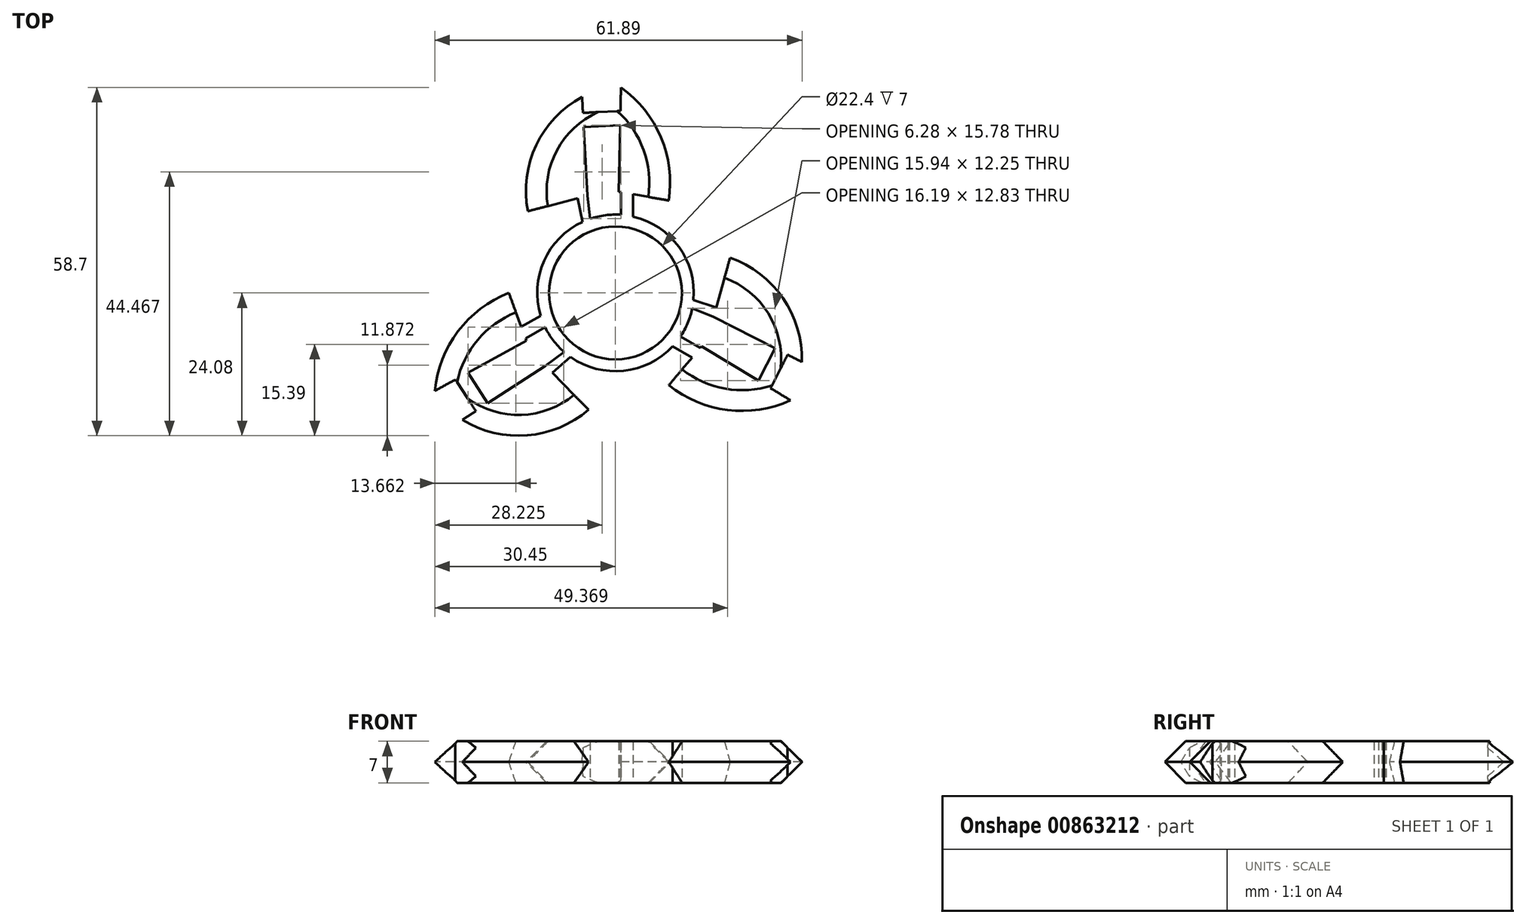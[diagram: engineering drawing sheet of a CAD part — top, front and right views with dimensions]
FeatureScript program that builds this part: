
annotation { "Feature Type Name" : "Feature", "Feature Type Description" : "" }
export const myFeature = defineFeature(function(context is Context, id is Id, definition is map)
    precondition{}
    {
        {
            var Q0;
            Q0=qCreatedBy(makeId("Top.planeOp"),FACE);
            var sketch = newSketch(context, id + "F0", { "sketchPlane" : qUnion([Q0])});
            skCircle(sketch, "E0", {"center": v(0, 0) * mm, "radius": 11.2 * mm});
            skCircle(sketch, "E1", {"center": v(0, 0) * mm, "radius": 13.2 * mm});
            skLineSegment(sketch, "E2", {"start": v(-11.8, -12.3) * mm, "end": v(-4.52, -19.69) * mm});
            skLineSegment(sketch, "E3", {"start": v(-15.03, -8.08) * mm, "end": v(-17.98, 0) * mm});
            skLineSegment(sketch, "E4", {"start": v(-15.03, -8.08) * mm, "end": v(-30.45, -16.5) * mm});
            skLineSegment(sketch, "E5", {"start": v(-11.8, -12.3) * mm, "end": v(-25.8, -21.4) * mm});
            skArc(sketch, "E6", {"start": v(-17.98, 0) * mm, "mid": v(-26.55, -6.49) * mm, "end": v(-30.45, -16.5) * mm});
            skArc(sketch, "E7", {"start": v(-25.8, -21.4) * mm, "mid": v(-14.88, -24.02) * mm, "end": v(-4.52, -19.69) * mm});
            skLineSegment(sketch, "E8.1.0", {"start": v(14.51, -8.98) * mm, "end": v(8.99, -15.57) * mm});
            skArc(sketch, "E8.1.3", {"start": v(8.99, -15.57) * mm, "mid": v(18.9, -19.75) * mm, "end": v(29.52, -18.11) * mm});
            skLineSegment(sketch, "E8.1.4", {"start": v(14.51, -8.98) * mm, "end": v(29.52, -18.11) * mm});
            skLineSegment(sketch, "E8.1.5", {"start": v(16.55, -4.07) * mm, "end": v(31.43, -11.65) * mm});
            skLineSegment(sketch, "E8.1.7", {"start": v(16.55, -4.07) * mm, "end": v(19.31, 5.93) * mm});
            skArc(sketch, "E8.1.9", {"start": v(31.43, -11.65) * mm, "mid": v(28.24, -0.88) * mm, "end": v(19.31, 5.93) * mm});
            skLineSegment(sketch, "E8.2.0", {"start": v(0.52, 17.06) * mm, "end": v(8.99, 15.57) * mm});
            skArc(sketch, "E8.2.3", {"start": v(8.99, 15.57) * mm, "mid": v(7.65, 26.24) * mm, "end": v(0.93, 34.62) * mm});
            skLineSegment(sketch, "E8.2.4", {"start": v(0.52, 17.06) * mm, "end": v(0.93, 34.62) * mm});
            skLineSegment(sketch, "E8.2.5", {"start": v(-4.75, 16.37) * mm, "end": v(-5.63, 33.04) * mm});
            skLineSegment(sketch, "E8.2.7", {"start": v(-4.75, 16.37) * mm, "end": v(-14.79, 13.76) * mm});
            skArc(sketch, "E8.2.9", {"start": v(-5.63, 33.04) * mm, "mid": v(-13.36, 24.9) * mm, "end": v(-14.79, 13.76) * mm});
            skPoint(sketch, "E9.end.orphan", {"position": v(-15.78, -5.85) * mm});
            skPoint(sketch, "E10.start.orphan", {"position": v(-11.83, -5.85) * mm});
            skPoint(sketch, "E11.startSnap0", {"position": v(4.76, 16.31) * mm});
            skPoint(sketch, "E12.orphan", {"position": v(-9.55, -5.85) * mm});
            skPoint(sketch, "E13.end.orphan", {"position": v(13.36, -14.64) * mm});
            skPoint(sketch, "E11.start.orphan", {"position": v(4.76, 17.14) * mm});
            skLineSegment(sketch, "E14", {"start": v(0.91, 17.67) * mm, "end": v(0.91, 12.44) * mm});
            skLineSegment(sketch, "E15", {"start": v(2.98, 17.14) * mm, "end": v(2.98, 12.22) * mm});
            skLineSegment(sketch, "E16", {"start": v(-4.75, 16.37) * mm, "end": v(-4.13, 11.53) * mm});
            skLineSegment(sketch, "E17", {"start": v(-5.43, 11.37) * mm, "end": v(-6.5, 16.65) * mm});
            skLineSegment(sketch, "E18.1.0", {"start": v(-11.8, -12.3) * mm, "end": v(-7.92, -9.34) * mm});
            skLineSegment(sketch, "E18.1.1", {"start": v(-7.13, -10.4) * mm, "end": v(-11.17, -13.96) * mm});
            skLineSegment(sketch, "E18.2.0", {"start": v(16.55, -4.07) * mm, "end": v(12.05, -2.19) * mm});
            skLineSegment(sketch, "E18.2.1", {"start": v(12.57, -0.98) * mm, "end": v(17.67, -2.7) * mm});
            skLineSegment(sketch, "E19.1.0", {"start": v(-15.76, -8.05) * mm, "end": v(-11.23, -5.43) * mm});
            skLineSegment(sketch, "E19.1.1", {"start": v(-16.33, -6) * mm, "end": v(-12.07, -3.53) * mm});
            skLineSegment(sketch, "E19.2.0", {"start": v(14.85, -9.63) * mm, "end": v(10.32, -7.01) * mm});
            skLineSegment(sketch, "E19.2.1", {"start": v(13.36, -11.15) * mm, "end": v(9.1, -8.68) * mm});
            skLineSegment(sketch, "E20", {"start": v(0.84, 30.67) * mm, "end": v(-5.49, 30.34) * mm});
            skLineSegment(sketch, "E21", {"start": v(-5.36, 27.95) * mm, "end": v(0.78, 28.28) * mm});
            skLineSegment(sketch, "E22.1.0", {"start": v(-26.98, -14.61) * mm, "end": v(-23.53, -19.92) * mm});
            skLineSegment(sketch, "E22.1.1", {"start": v(-21.53, -18.62) * mm, "end": v(-24.88, -13.46) * mm});
            skLineSegment(sketch, "E22.2.0", {"start": v(26.15, -16.06) * mm, "end": v(29.02, -10.42) * mm});
            skLineSegment(sketch, "E22.2.1", {"start": v(26.9, -9.33) * mm, "end": v(24.1, -14.82) * mm});
            skSolve(sketch);
        }
        {
            var Q0;
            {var subQ0=sQuery(id+"F0.wireOp",EDGE,"E20");Q0=makeQuery(id+"F0.imprint","IMPRINT",FACE,{"disambiguationData":[TD([[makeQuery(id+"F0.imprint","IMPRINT",EDGE,{"derivedFrom":subQ0}),1.0]])]});}
            var Q1;
            {var subQ4=sQuery(id+"F0.wireOp",EDGE,"E8.2.9");Q1=makeQuery(id+"F0.imprint","IMPRINT",FACE,{"disambiguationData":[TD([[makeQuery(id+"F0.imprint","IMPRINT",EDGE,{"derivedFrom":subQ4}),1.0]])]});}
            var Q2;
            {var subQ0=sQuery(id+"F0.wireOp",EDGE,"E17");var subQ1=sQuery(id+"F0.wireOp",EDGE,"E1");var subQ2=makeQuery(id+"F0.imprint","INTERSECT",VERTEX,{"derivedFrom":[subQ1,subQ0]});Q2=makeQuery(id+"F0.imprint","IMPRINT",FACE,{"disambiguationData":[TD([[makeQuery(id+"F0.imprint","IMPRINT",EDGE,{"disambiguationData":[TD([[subQ2,1.0]])],"derivedFrom":subQ1}),-1.0]])]});}
            var Q3;
            {var subQ0=sQuery(id+"F0.wireOp",EDGE,"E8.2.3");Q3=makeQuery(id+"F0.imprint","IMPRINT",FACE,{"disambiguationData":[TD([[makeQuery(id+"F0.imprint","IMPRINT",EDGE,{"derivedFrom":subQ0}),1.0]])]});}
            var Q4;
            {var subQ0=sQuery(id+"F0.wireOp",EDGE,"E15");var subQ1=sQuery(id+"F0.wireOp",EDGE,"E1");var subQ2=makeQuery(id+"F0.imprint","INTERSECT",VERTEX,{"derivedFrom":[subQ1,subQ0]});Q4=makeQuery(id+"F0.imprint","IMPRINT",FACE,{"disambiguationData":[TD([[makeQuery(id+"F0.imprint","IMPRINT",EDGE,{"disambiguationData":[TD([[subQ2,-1.0]])],"derivedFrom":subQ1}),-1.0]])]});}
            var Q5;
            Q5=makeQuery(id+"F0.imprint","IMPRINT",FACE,{"disambiguationData":[TD([[makeQuery(id+"F0.imprint","IMPRINT",EDGE,{"derivedFrom":sQuery(id+"F0.wireOp",EDGE,"E0")}),-1.0]])]});
            var Q6;
            {var subQ4=sQuery(id+"F0.wireOp",EDGE,"E6");Q6=makeQuery(id+"F0.imprint","IMPRINT",FACE,{"disambiguationData":[TD([[makeQuery(id+"F0.imprint","IMPRINT",EDGE,{"derivedFrom":subQ4}),1.0]])]});}
            var Q7;
            {var subQ0=sQuery(id+"F0.wireOp",EDGE,"E19.1.1");var subQ1=sQuery(id+"F0.wireOp",EDGE,"E1");var subQ2=makeQuery(id+"F0.imprint","INTERSECT",VERTEX,{"derivedFrom":[subQ1,subQ0]});Q7=makeQuery(id+"F0.imprint","IMPRINT",FACE,{"disambiguationData":[TD([[makeQuery(id+"F0.imprint","IMPRINT",EDGE,{"disambiguationData":[TD([[subQ2,-1.0]])],"derivedFrom":subQ1}),-1.0]])]});}
            var Q8;
            {var subQ0=sQuery(id+"F0.wireOp",EDGE,"E18.1.1");var subQ1=sQuery(id+"F0.wireOp",EDGE,"E1");var subQ2=makeQuery(id+"F0.imprint","INTERSECT",VERTEX,{"derivedFrom":[subQ1,subQ0]});Q8=makeQuery(id+"F0.imprint","IMPRINT",FACE,{"disambiguationData":[TD([[makeQuery(id+"F0.imprint","IMPRINT",EDGE,{"disambiguationData":[TD([[subQ2,1.0]])],"derivedFrom":subQ1}),-1.0]])]});}
            var Q9;
            {var subQ5=sQuery(id+"F0.wireOp",EDGE,"E7");Q9=makeQuery(id+"F0.imprint","IMPRINT",FACE,{"disambiguationData":[TD([[makeQuery(id+"F0.imprint","IMPRINT",EDGE,{"derivedFrom":subQ5}),1.0]])]});}
            var Q10;
            {var subQ0=sQuery(id+"F0.wireOp",EDGE,"E22.1.0");Q10=makeQuery(id+"F0.imprint","IMPRINT",FACE,{"disambiguationData":[TD([[makeQuery(id+"F0.imprint","IMPRINT",EDGE,{"derivedFrom":subQ0}),1.0]])]});}
            var Q11;
            {var subQ0=sQuery(id+"F0.wireOp",EDGE,"E19.2.1");var subQ1=sQuery(id+"F0.wireOp",EDGE,"E1");var subQ2=makeQuery(id+"F0.imprint","INTERSECT",VERTEX,{"derivedFrom":[subQ1,subQ0]});Q11=makeQuery(id+"F0.imprint","IMPRINT",FACE,{"disambiguationData":[TD([[makeQuery(id+"F0.imprint","IMPRINT",EDGE,{"disambiguationData":[TD([[subQ2,-1.0]])],"derivedFrom":subQ1}),-1.0]])]});}
            var Q12;
            {var subQ0=sQuery(id+"F0.wireOp",EDGE,"E8.1.3");Q12=makeQuery(id+"F0.imprint","IMPRINT",FACE,{"disambiguationData":[TD([[makeQuery(id+"F0.imprint","IMPRINT",EDGE,{"derivedFrom":subQ0}),1.0]])]});}
            var Q13;
            {var subQ0=sQuery(id+"F0.wireOp",EDGE,"E22.2.0");Q13=makeQuery(id+"F0.imprint","IMPRINT",FACE,{"disambiguationData":[TD([[makeQuery(id+"F0.imprint","IMPRINT",EDGE,{"derivedFrom":subQ0}),1.0]])]});}
            var Q14;
            {var subQ4=sQuery(id+"F0.wireOp",EDGE,"E8.1.9");Q14=makeQuery(id+"F0.imprint","IMPRINT",FACE,{"disambiguationData":[TD([[makeQuery(id+"F0.imprint","IMPRINT",EDGE,{"derivedFrom":subQ4}),1.0]])]});}
            var Q15;
            {var subQ0=sQuery(id+"F0.wireOp",EDGE,"E18.2.1");var subQ1=sQuery(id+"F0.wireOp",EDGE,"E1");var subQ2=makeQuery(id+"F0.imprint","INTERSECT",VERTEX,{"derivedFrom":[subQ1,subQ0]});Q15=makeQuery(id+"F0.imprint","IMPRINT",FACE,{"disambiguationData":[TD([[makeQuery(id+"F0.imprint","IMPRINT",EDGE,{"disambiguationData":[TD([[subQ2,1.0]])],"derivedFrom":subQ1}),-1.0]])]});}
            extrude(context, id + "F1", {"entities" : qUnion([Q0, Q1, Q2, Q3, Q4, Q5, Q6, Q7, Q8, Q9, Q10, Q11, Q12, Q13, Q14, Q15]), "depth" : 7 * mm, "offsetDistance" : 25 * mm});
        }
        {
            var Q0;
            Q0=makeQuery(id+"F1.opExtrude","CAP_EDGE",EDGE,{"disambiguationData":[OSD([sQuery(id+"F0.wireOp",EDGE,"E8.2.9")])],"isStart":false});
            var Q1;
            Q1=makeQuery(id+"F1.opExtrude","CAP_EDGE",EDGE,{"disambiguationData":[OSD([sQuery(id+"F0.wireOp",EDGE,"E8.2.3")])],"isStart":false});
            var Q2;
            Q2=makeQuery(id+"F1.opExtrude","CAP_EDGE",EDGE,{"disambiguationData":[OSD([sQuery(id+"F0.wireOp",EDGE,"E8.1.9")])],"isStart":false});
            var Q3;
            Q3=makeQuery(id+"F1.opExtrude","CAP_EDGE",EDGE,{"disambiguationData":[OSD([sQuery(id+"F0.wireOp",EDGE,"E8.1.3")])],"isStart":false});
            var Q4;
            Q4=makeQuery(id+"F1.opExtrude","CAP_EDGE",EDGE,{"disambiguationData":[OSD([sQuery(id+"F0.wireOp",EDGE,"E7")])],"isStart":false});
            var Q5;
            Q5=makeQuery(id+"F1.opExtrude","CAP_EDGE",EDGE,{"disambiguationData":[OSD([sQuery(id+"F0.wireOp",EDGE,"E6")])],"isStart":false});
            chamfer(context, id + "F2", {"entities" : qUnion([Q0, Q1, Q2, Q3, Q4, Q5]), "width" : 3.5 * mm, "tangentPropagation" : true});
        }
        {
            var Q0;
            Q0=makeQuery(id+"F1.opExtrude","CAP_EDGE",EDGE,{"disambiguationData":[OSD([sQuery(id+"F0.wireOp",EDGE,"E8.2.3")])],"isStart":true});
            var Q1;
            Q1=makeQuery(id+"F1.opExtrude","CAP_EDGE",EDGE,{"disambiguationData":[OSD([sQuery(id+"F0.wireOp",EDGE,"E8.2.9")])],"isStart":true});
            var Q2;
            Q2=makeQuery(id+"F1.opExtrude","CAP_EDGE",EDGE,{"disambiguationData":[OSD([sQuery(id+"F0.wireOp",EDGE,"E6")])],"isStart":true});
            var Q3;
            Q3=makeQuery(id+"F1.opExtrude","CAP_EDGE",EDGE,{"disambiguationData":[OSD([sQuery(id+"F0.wireOp",EDGE,"E7")])],"isStart":true});
            var Q4;
            Q4=makeQuery(id+"F1.opExtrude","CAP_EDGE",EDGE,{"disambiguationData":[OSD([sQuery(id+"F0.wireOp",EDGE,"E8.1.3")])],"isStart":true});
            var Q5;
            Q5=makeQuery(id+"F1.opExtrude","CAP_EDGE",EDGE,{"disambiguationData":[OSD([sQuery(id+"F0.wireOp",EDGE,"E8.1.9")])],"isStart":true});
            chamfer(context, id + "F3", {"entities" : qUnion([Q0, Q1, Q2, Q3, Q4, Q5]), "width" : 3.5 * mm, "tangentPropagation" : true});
        }
    });
